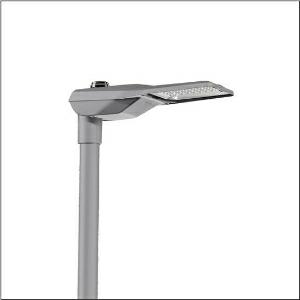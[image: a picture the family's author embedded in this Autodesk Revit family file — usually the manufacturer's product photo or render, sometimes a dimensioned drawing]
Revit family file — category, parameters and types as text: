
# Revit family: streetlight_sl_21_mini___p0_8a_5xe6u57n08jb_174f
name_source: partatom
category: Lighting Fixtures
units: mm (PartAtom-declared; Revit-internal decimal feet)

## family parameters
Cut with Voids When Loaded = No
Host = Face
Light Source = No
Part Type = Normal
Room Calculation Point = No
Round Connector Dimension = Use Diameter
Shared = No

## types (1)
- --- (1 x LED, 11130 lm, 87.3 W, 3000K)
    Apparent Load = 87 VA
    CIE Flux Codes = 36 69 97 100 100
    Color Rendering = 80
    Color Temperature = 3000K
    Default Elevation = 1800 mm
    Description = Streetlight SL 21 mini, mast luminaire, primary light control with lens, of PMMA, primary optical cover: cover, of toughened safety glass, transparent, light distribution: P0.8a, light emission: direct distribution, primary light characteristic: asymmetric, installation type: side-entry, LED, 3G 2.5mm², High Power LED, rated luminous flux: 11.130lm, luminous efficacy: 128lm/W, light colour: 830, colour temperature: 3000K, control gear: NEMA (7pin), control: flexible luminous flux parameterisation, time-dependent luminous flux control, constant luminous flux control, pre-setting: linear dimming characteristic, overheat protection, mains connection: 230..240V, AC, 50/60Hz, connection cable pre-assembled, cable length: 10,5m, wiring characteristics: H05VV-F, start of lifetime: 87W, end of service life: 90W, reduction: 40W, luminaire housing, of diecast aluminium (EN AC-44300), powder-coated, Siteco® metallic grey (DB 702S), corrosivity category C5 mid according to DIN EN ISO 12944, multi-level sealing system, sealing non-destructively replaceable, inclination adjustable: 0°, 5°, 10°, 15°, length: 628mm, width: 235mm, height: 110mm, spigot size: 42mm (side-entry), mounting height: 4..8m, protection rating (complete): IP66, insulation class (complete): insulation class I (protective earthing), certification: CE, ENEC, ENEC+, VDE, impact resistance: IK09, permissible operating ambient temperature for outdoor applications: -40..+50°C, standard-compliant lighting for roads and squares, packaging unit: 1 piece

Light Distribution: P0.8a
    Height = 110 mm
    Lamp = 1 x LED
    Lamp Light Flux = 11130 lm
    Lamp Power = 87.3 W
    Lamp count = 1
    Length = 625 mm
    Luminous efficacy = 127 lm/W
    Manufacturer = Siteco
    ModVariant = No
    Model = 5XE6U57N08JB
    Number of Poles = 1
    OnlyDefault = Yes
    Power Factor = 1
    Product Name = Streetlight SL 21 mini | P0.8a
    Product group = mast luminaire | pylon top
    ProductGroupID = 6100
    Protection Class = Protection class I
    Protection Degree = IP 66
    RLX_Detail_Level = 1
    RLX_Emergency_Light_Flux = 0 lm
    RLX_Emergency_Type = 0
    RLX_Emergency_Type_DB = No
    RlxData = <blob elided: 93625 chars, md5=e9004369>
    Socket = socket
    Standby Power = 0 W
    System Light Flux = 11130 lm
    System Power = 87 W
    Type Comments = factory setting: luminous flux: 100 % | dim-lin: 254 | 915 mA
    Type Image = l_1294379.jpg
    URL = http://relux.com
    VarID = @adj_068832
    Voltage = 0 V
    Weight = 0.00 kg
    Width = 234 mm

## geometry (parser evidence)
native form markers: Blend x4, Sweep x9
no freeform markers — native parametric forms only
